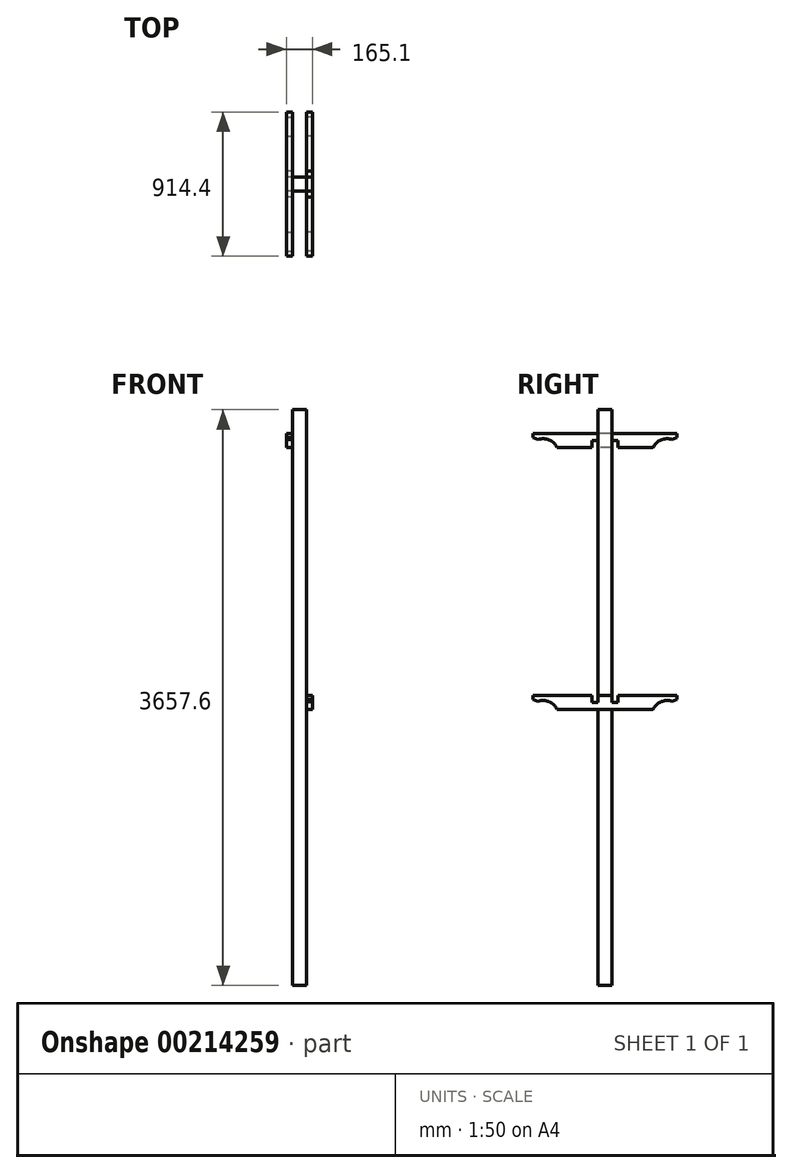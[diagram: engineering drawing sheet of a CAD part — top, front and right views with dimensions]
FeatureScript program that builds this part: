
annotation { "Feature Type Name" : "Feature", "Feature Type Description" : "" }
export const myFeature = defineFeature(function(context is Context, id is Id, definition is map)
    precondition{}
    {
        {
            var Q0;
            Q0=qCreatedBy(makeId("Top.planeOp"),FACE);
            var sketch = newSketch(context, id + "F0", { "sketchPlane" : qUnion([Q0])});
            skLineSegment(sketch, "E0.bottom", {"start": v(44.45, -44.45) * mm, "end": v(-44.45, -44.45) * mm});
            skLineSegment(sketch, "E0.top", {"start": v(44.45, 44.45) * mm, "end": v(-44.45, 44.45) * mm});
            skLineSegment(sketch, "E0.left", {"start": v(44.45, -44.45) * mm, "end": v(44.45, 44.45) * mm});
            skLineSegment(sketch, "E0.right", {"start": v(-44.45, -44.45) * mm, "end": v(-44.45, 44.45) * mm});
            skPoint(sketch, "E0.middle", {"position": v(0, 0) * mm});
            skSolve(sketch);
        }
        {
            var Q0;
            Q0=makeQuery(id+"F0.imprint","IMPRINT",FACE,{"disambiguationData":[TD([[makeQuery(id+"F0.imprint","IMPRINT",EDGE,{"derivedFrom":sQuery(id+"F0.wireOp",EDGE,"E0.bottom")}),-1.0]])]});
            extrude(context, id + "F1", {"entities" : qUnion([Q0]), "depth" : 3657.6 * mm});
        }
        {
            var Q0;
            Q0=makeQuery(id+"F1.opExtrude","SWEPT_FACE",FACE,{"disambiguationData":[OSD([sQuery(id+"F0.wireOp",EDGE,"E0.right")])]});
            var sketch = newSketch(context, id + "F2", { "sketchPlane" : qUnion([Q0])});
            skLineSegment(sketch, "E1.bottom", {"start": v(-457.2, 3505.2) * mm, "end": v(457.2, 3505.2) * mm});
            skLineSegment(sketch, "E1.top", {"start": v(-304.8, 3416.3) * mm, "end": v(304.8, 3416.3) * mm});
            skLineSegment(sketch, "E1.left", {"start": v(-457.2, 3505.2) * mm, "end": v(-457.2, 3479.8) * mm});
            skLineSegment(sketch, "E1.right", {"start": v(457.2, 3505.2) * mm, "end": v(457.2, 3479.8) * mm});
            skPoint(sketch, "E2", {"position": v(0, 3505.2) * mm});
            skPoint(sketch, "E2.positionSnap0", {"position": v(0, 3505.2) * mm});
            skPoint(sketch, "E3", {"position": v(0, 3657.6) * mm});
            skArc(sketch, "E4", {"start": v(425.45, 3467.34) * mm, "mid": v(355.39, 3464.84) * mm, "end": v(304.8, 3416.3) * mm});
            skLineSegment(sketch, "E5", {"start": v(425.45, 3467.34) * mm, "end": v(457.2, 3479.8) * mm});
            skLineSegment(sketch, "E6", {"start": v(0, 3505.2) * mm, "end": v(0, 3416.3) * mm, "construction": true});
            skArc(sketch, "E7.MirrorCS", {"start": v(-425.45, 3467.34) * mm, "mid": v(-355.39, 3464.84) * mm, "end": v(-304.8, 3416.3) * mm});
            skLineSegment(sketch, "E8.MirrorCS", {"start": v(-425.45, 3467.34) * mm, "end": v(-457.2, 3479.8) * mm});
            skSolve(sketch);
        }
        {
            var Q0;
            {var subQ0=sQuery(id+"F2.wireOp",EDGE,"E1.left");Q0=makeQuery(id+"F2.imprint","IMPRINT",FACE,{"disambiguationData":[TD([[makeQuery(id+"F2.imprint","IMPRINT",EDGE,{"derivedFrom":subQ0}),1.0]])]});}
            var Q1;
            {var subQ0=sQuery(id+"F2.wireOp",EDGE,"E1.right");Q1=makeQuery(id+"F2.imprint","IMPRINT",FACE,{"disambiguationData":[TD([[makeQuery(id+"F2.imprint","IMPRINT",EDGE,{"derivedFrom":subQ0}),-1.0]])]});}
            var Q2;
            {var subQ0=sQuery(id+"F2.wireOp",EDGE,"E1.bottom");var subQ1=sQuery(id+"F0.wireOp",EDGE,"E0.right");var subQ2=makeQuery(id+"F1.opExtrude","SWEPT_EDGE",EDGE,{"disambiguationData":[OSD([sQuery(id+"F0.wireOp",EDGE,"E0.top"),subQ1])]});var subQ3=makeQuery(id+"F2.imprint","INTERSECT",VERTEX,{"derivedFrom":[subQ2,subQ0]});Q2=makeQuery(id+"F2.imprint","IMPRINT",FACE,{"disambiguationData":[TD([[makeQuery(id+"F2.imprint","IMPRINT",EDGE,{"disambiguationData":[TD([[subQ3,-1.0]])],"derivedFrom":subQ0}),-1.0]])]});}
            extrude(context, id + "F3", {"entities" : qUnion([Q0, Q1, Q2]), "depth" : 38.1 * mm});
        }
        {
            var Q0;
            Q0=makeQuery(id+"F3.opExtrude","CAP_FACE",FACE,{"disambiguationData":[OSD([sQuery(id+"F2.wireOp",EDGE,"E1.bottom"),sQuery(id+"F2.wireOp",EDGE,"E1.top"),sQuery(id+"F2.wireOp",EDGE,"E1.left"),sQuery(id+"F2.wireOp",EDGE,"E1.right"),sQuery(id+"F2.wireOp",EDGE,"E4"),sQuery(id+"F2.wireOp",EDGE,"E5"),sQuery(id+"F2.wireOp",EDGE,"E7.MirrorCS"),sQuery(id+"F2.wireOp",EDGE,"E8.MirrorCS")])],"isStart":false});
            var sketch = newSketch(context, id + "F4", { "sketchPlane" : qUnion([Q0])});
            skLineSegment(sketch, "E9", {"start": v(0, 3505.2) * mm, "end": v(0, 3416.3) * mm, "construction": true});
            skLineSegment(sketch, "E10", {"start": v(44.45, 3416.3) * mm, "end": v(44.45, 3460.75) * mm});
            skLineSegment(sketch, "E11", {"start": v(44.45, 3460.75) * mm, "end": v(82.55, 3460.75) * mm});
            skLineSegment(sketch, "E12", {"start": v(82.55, 3460.75) * mm, "end": v(82.55, 3416.3) * mm});
            skPoint(sketch, "E13", {"position": v(0, 3460.75) * mm});
            skLineSegment(sketch, "E14.MirrorCS", {"start": v(-44.45, 3416.3) * mm, "end": v(-44.45, 3460.75) * mm});
            skLineSegment(sketch, "E15.MirrorCS", {"start": v(-44.45, 3460.75) * mm, "end": v(-82.55, 3460.75) * mm});
            skLineSegment(sketch, "E16.MirrorCS", {"start": v(-82.55, 3460.75) * mm, "end": v(-82.55, 3416.3) * mm});
            skSolve(sketch);
        }
        {
            var Q0;
            {var subQ0=sQuery(id+"F4.wireOp",EDGE,"E10");Q0=makeQuery(id+"F4.imprint","IMPRINT",FACE,{"disambiguationData":[TD([[makeQuery(id+"F4.imprint","IMPRINT",EDGE,{"derivedFrom":subQ0}),-1.0]])]});}
            extrude(context, id + "F5", {"entities" : qUnion([Q0]), "operationType" : NewBodyOperationType.REMOVE, "oppositeDirection" : true, "depth" : 254 * mm});
        }
        {
            var Q0;
            {var subQ0=sQuery(id+"F4.wireOp",EDGE,"E14.MirrorCS");Q0=makeQuery(id+"F4.imprint","IMPRINT",FACE,{"disambiguationData":[TD([[makeQuery(id+"F4.imprint","IMPRINT",EDGE,{"derivedFrom":subQ0}),1.0]])]});}
            extrude(context, id + "F6", {"entities" : qUnion([Q0]), "operationType" : NewBodyOperationType.REMOVE, "oppositeDirection" : true, "depth" : 254 * mm});
        }
        {
            var Q0;
            Q0=makeQuery(id+"F1.opExtrude","SWEPT_FACE",FACE,{"disambiguationData":[OSD([sQuery(id+"F0.wireOp",EDGE,"E0.left")])]});
            var sketch = newSketch(context, id + "F7", { "sketchPlane" : qUnion([Q0])});
            skLineSegment(sketch, "E17.bottom", {"start": v(-457.2, 1842.63) * mm, "end": v(457.2, 1842.63) * mm});
            skLineSegment(sketch, "E17.top", {"start": v(-304.8, 1753.73) * mm, "end": v(304.8, 1753.73) * mm});
            skLineSegment(sketch, "E17.left", {"start": v(-457.2, 1842.63) * mm, "end": v(-457.2, 1817.23) * mm});
            skLineSegment(sketch, "E17.right", {"start": v(457.2, 1842.63) * mm, "end": v(457.2, 1817.23) * mm});
            skPoint(sketch, "E18", {"position": v(0, 1842.63) * mm});
            skPoint(sketch, "E18.positionSnap0", {"position": v(0, 1842.63) * mm});
            skPoint(sketch, "E19", {"position": v(0, 1995.03) * mm});
            skArc(sketch, "E20", {"start": v(425.45, 1804.77) * mm, "mid": v(355.39, 1802.27) * mm, "end": v(304.8, 1753.73) * mm});
            skLineSegment(sketch, "E21", {"start": v(425.45, 1804.77) * mm, "end": v(457.2, 1817.23) * mm});
            skLineSegment(sketch, "E22", {"start": v(0, 1842.63) * mm, "end": v(0, 1753.73) * mm, "construction": true});
            skArc(sketch, "E23.MirrorCS", {"start": v(-425.45, 1804.77) * mm, "mid": v(-355.39, 1802.27) * mm, "end": v(-304.8, 1753.73) * mm});
            skLineSegment(sketch, "E24.MirrorCS", {"start": v(-425.45, 1804.77) * mm, "end": v(-457.2, 1817.23) * mm});
            skSolve(sketch);
        }
        {
            var Q0;
            {var subQ1=sQuery(id+"F7.wireOp",EDGE,"E17.left");Q0=makeQuery(id+"F7.imprint","IMPRINT",FACE,{"disambiguationData":[TD([[makeQuery(id+"F7.imprint","IMPRINT",EDGE,{"derivedFrom":subQ1}),1.0]])]});}
            var Q1;
            {var subQ0=sQuery(id+"F7.wireOp",EDGE,"E17.bottom");var subQ1=sQuery(id+"F0.wireOp",EDGE,"E0.left");var subQ2=makeQuery(id+"F1.opExtrude","SWEPT_EDGE",EDGE,{"disambiguationData":[OSD([sQuery(id+"F0.wireOp",EDGE,"E0.bottom"),subQ1])]});var subQ3=makeQuery(id+"F7.imprint","INTERSECT",VERTEX,{"derivedFrom":[subQ2,subQ0]});Q1=makeQuery(id+"F7.imprint","IMPRINT",FACE,{"disambiguationData":[TD([[makeQuery(id+"F7.imprint","IMPRINT",EDGE,{"disambiguationData":[TD([[subQ3,-1.0]])],"derivedFrom":subQ0}),-1.0]])]});}
            var Q2;
            {var subQ1=sQuery(id+"F7.wireOp",EDGE,"E17.right");Q2=makeQuery(id+"F7.imprint","IMPRINT",FACE,{"disambiguationData":[TD([[makeQuery(id+"F7.imprint","IMPRINT",EDGE,{"derivedFrom":subQ1}),-1.0]])]});}
            extrude(context, id + "F8", {"entities" : qUnion([Q0, Q1, Q2]), "depth" : 38.1 * mm});
        }
        {
            var Q0;
            Q0=makeQuery(id+"F8.opExtrude","CAP_FACE",FACE,{"disambiguationData":[OSD([sQuery(id+"F7.wireOp",EDGE,"E17.bottom"),sQuery(id+"F7.wireOp",EDGE,"E17.top"),sQuery(id+"F7.wireOp",EDGE,"E17.left"),sQuery(id+"F7.wireOp",EDGE,"E17.right"),sQuery(id+"F7.wireOp",EDGE,"E20"),sQuery(id+"F7.wireOp",EDGE,"E21"),sQuery(id+"F7.wireOp",EDGE,"E23.MirrorCS"),sQuery(id+"F7.wireOp",EDGE,"E24.MirrorCS")])],"isStart":false});
            var sketch = newSketch(context, id + "F9", { "sketchPlane" : qUnion([Q0])});
            skLineSegment(sketch, "E25", {"start": v(0, 1842.63) * mm, "end": v(0, 1753.73) * mm, "construction": true});
            skLineSegment(sketch, "E26", {"start": v(44.45, 1842.63) * mm, "end": v(44.45, 1798.18) * mm});
            skLineSegment(sketch, "E27", {"start": v(44.45, 1798.18) * mm, "end": v(82.55, 1798.18) * mm});
            skLineSegment(sketch, "E28", {"start": v(82.55, 1798.18) * mm, "end": v(82.55, 1842.63) * mm});
            skPoint(sketch, "E29", {"position": v(0, 1798.18) * mm});
            skLineSegment(sketch, "E30.MirrorCS", {"start": v(-44.45, 1842.63) * mm, "end": v(-44.45, 1798.18) * mm});
            skLineSegment(sketch, "E31.MirrorCS", {"start": v(-44.45, 1798.18) * mm, "end": v(-82.55, 1798.18) * mm});
            skLineSegment(sketch, "E32.MirrorCS", {"start": v(-82.55, 1798.18) * mm, "end": v(-82.55, 1842.63) * mm});
            skSolve(sketch);
        }
        {
            var Q0;
            {var subQ0=sQuery(id+"F9.wireOp",EDGE,"E30.MirrorCS");Q0=makeQuery(id+"F9.imprint","IMPRINT",FACE,{"disambiguationData":[TD([[makeQuery(id+"F9.imprint","IMPRINT",EDGE,{"derivedFrom":subQ0}),-1.0]])]});}
            var Q1;
            {var subQ0=sQuery(id+"F9.wireOp",EDGE,"E26");Q1=makeQuery(id+"F9.imprint","IMPRINT",FACE,{"disambiguationData":[TD([[makeQuery(id+"F9.imprint","IMPRINT",EDGE,{"derivedFrom":subQ0}),1.0]])]});}
            extrude(context, id + "F10", {"entities" : qUnion([Q0, Q1]), "operationType" : NewBodyOperationType.REMOVE, "oppositeDirection" : true, "depth" : 254 * mm});
        }
    });
